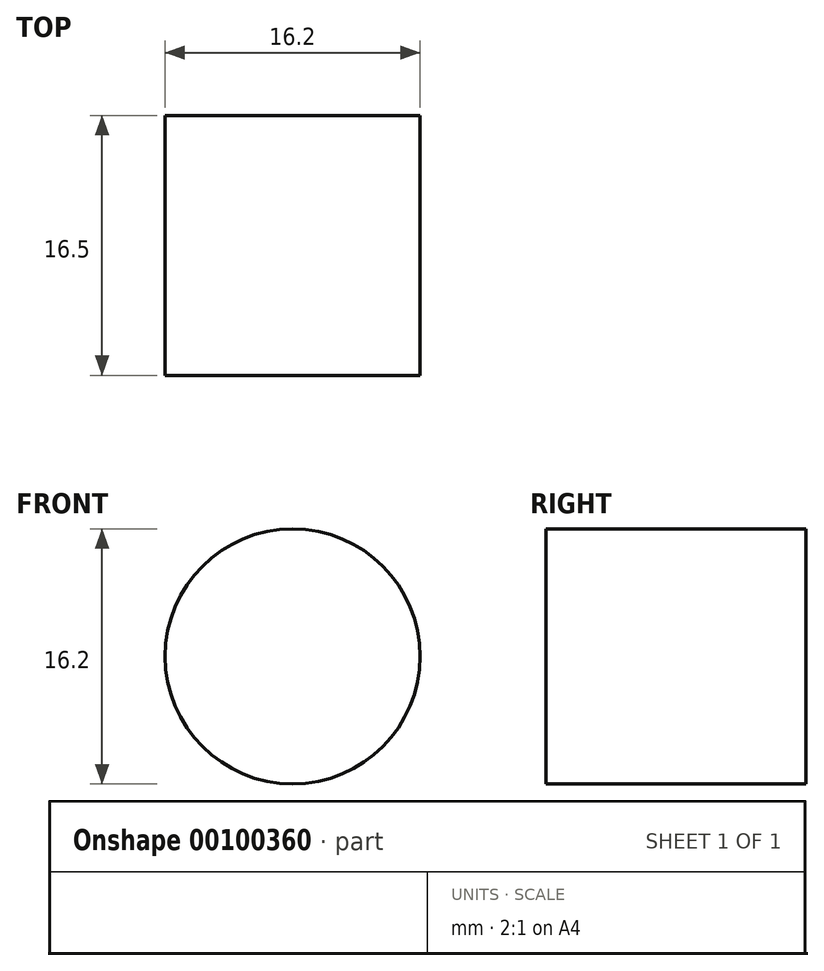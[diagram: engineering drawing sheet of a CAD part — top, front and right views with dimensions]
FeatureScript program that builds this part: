
annotation { "Feature Type Name" : "Feature", "Feature Type Description" : "" }
export const myFeature = defineFeature(function(context is Context, id is Id, definition is map)
    precondition{}
    {
        {
            var Q0;
            Q0=qCreatedBy(makeId("Front.planeOp"),FACE);
            var sketch = newSketch(context, id + "F0", { "sketchPlane" : qUnion([Q0])});
            skCircle(sketch, "E0", {"center": v(0, 0) * mm, "radius": 8.1 * mm});
            skSolve(sketch);
        }
        {
            var Q0;
            Q0=makeQuery(id+"F0.imprint","IMPRINT",FACE,{"disambiguationData":[TD([[makeQuery(id+"F0.imprint","IMPRINT",EDGE,{"derivedFrom":sQuery(id+"F0.wireOp",EDGE,"E0")}),1.0]])]});
            extrude(context, id + "F1", {"entities" : qUnion([Q0]), "depth" : 16.5 * mm});
        }
    });
